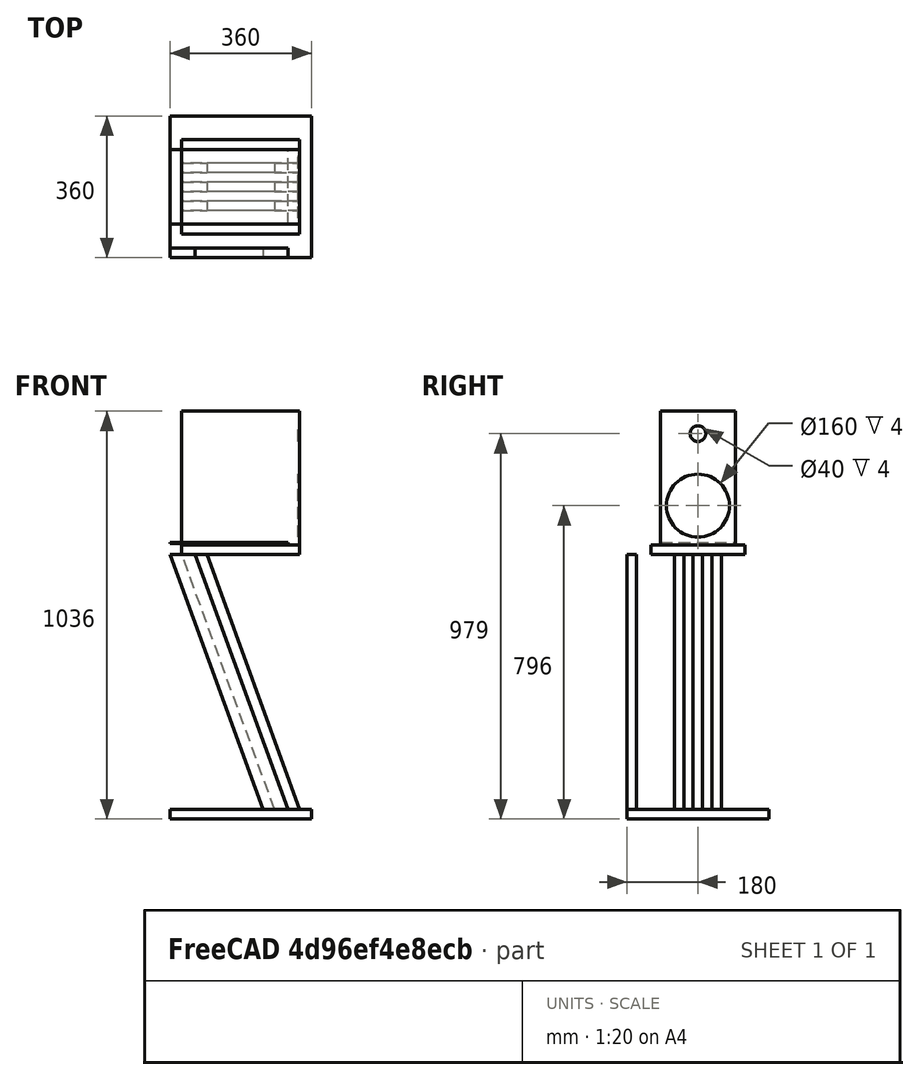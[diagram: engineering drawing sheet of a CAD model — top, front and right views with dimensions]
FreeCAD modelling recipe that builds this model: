
FCSTD DOCUMENT  (FreeCAD 0.18.4R)
Label: v3_3
License: All rights reserved
LicenseURL: http://en.wikipedia.org/wiki/All_rights_reserved
objects: Part::Box×6, Raytracing::RayFeature×6, Part::Feature×3, Part::Cylinder×2, Part::Cut×2, Part::MultiCommon×1, Raytracing::RayProject×1
note: 14 computed .brp shape members not serialized (recipe doc carries the construction recipe); baked Part::Feature solids carry a one-line shape summary decoded from their .brp

FEATURE [Part::Box] Box  label="Bottom"
  AttacherType = Attacher::AttachEngine3D
  Height = 24
  Length = 360
  Width = 360
FEATURE [Part::Box] Box003  label="SlipMate"
  AttacherType = Attacher::AttachEngine3D
  Height = 3
  Length = 300
  Placement = pos=(0,85,700) rot=(0,0,1;0rad)
  Width = 190
FEATURE [Part::Box] Box006  label="Speaker003"
  AttacherType = Attacher::AttachEngine3D
  Height = 340
  Length = 300
  Placement = pos=(0,0,850) rot=(0,0,1;0rad)
  Width = 190
FEATURE [Part::Cylinder] Cylinder002
  Angle = 360
  AttacherType = Attacher::AttachEngine3D
  Height = 10
  Placement = pos=(296,95,950) rot=(0,1,0;1.5708rad)
  Radius = 80
FEATURE [Part::Cut] Cut003
  Base = -> Box006
  Tool = -> Cylinder002
FEATURE [Part::Cylinder] Cylinder003
  Angle = 360
  AttacherType = Attacher::AttachEngine3D
  Height = 10
  Placement = pos=(296,95,1133) rot=(0,1,0;1.5708rad)
  Radius = 20
FEATURE [Part::Cut] Cut002  label="Speaker002"
  Base = -> Cut003
  Placement = pos=(30,85,-154) rot=(0,0,1;0rad)
  Tool = -> Cylinder003
FEATURE [Part::Box] Box012  label="Top"
  AttacherType = Attacher::AttachEngine3D
  Height = 24
  Length = 300
  Placement = pos=(30,60,672) rot=(0,0,1;0rad)
  Width = 240
FEATURE [Part::Box] Box015  label="Cube"
  AttacherType = Attacher::AttachEngine3D
  Height = 648
  Length = 300
  Placement = pos=(0,0,24) rot=(0,1,0;0rad)
  Width = 24
FEATURE [Part::Box] Box016  label="Cube007"
  AttacherType = Attacher::AttachEngine3D
  Height = 827
  Length = 60
  Placement = pos=(300,24,24) rot=(-0.173648,0,0.984808;3.14159rad)
  Width = 24
FEATURE [Part::MultiCommon] Common  label="Stand"
  Shapes = -> [Box015,Box016]
FEATURE [Part::Feature] Common_solid  label="Stand001"
  Placement = pos=(30,120,0) rot=(0,0,1;0rad)
  shape: bbox 299.7 x 24 x 648 mm, 6 faces (baked)
FEATURE [Part::Feature] Common_solid001  label="Stand002"
  Placement = pos=(30,168,0) rot=(0,0,1;0rad)
  shape: bbox 299.7 x 24 x 648 mm, 6 faces (baked)
FEATURE [Part::Feature] Common_solid002  label="Stand003"
  Placement = pos=(30,216,0) rot=(0,0,1;0rad)
  shape: bbox 299.7 x 24 x 648 mm, 6 faces (baked)
FEATURE [Raytracing::RayFeature] Common_solid_View
  Result = <blob: 3076 chars omitted>
  Source = -> Common_solid
  Transparency = 0
FEATURE [Raytracing::RayFeature] Common_solid002_View
  Result = <blob: 3038 chars omitted>
  Source = -> Common_solid002
  Transparency = 0
FEATURE [Raytracing::RayFeature] Common_solid001_View
  Result = <blob: 3038 chars omitted>
  Source = -> Common_solid001
  Transparency = 0
FEATURE [Raytracing::RayFeature] Box012_View
  Result = <blob: 2730 chars omitted>
  Source = -> Box012
  Transparency = 0
FEATURE [Raytracing::RayFeature] Box_View
  Result = <blob: 2628 chars omitted>
  Source = -> Box
  Transparency = 0
FEATURE [Raytracing::RayFeature] Cut002_View
  Result = <blob: 38202 chars omitted>
  Source = -> Cut002
  Transparency = 0
FEATURE [Raytracing::RayProject] PovProject
  Camera = // declares position and view direction\n\n// Generated by FreeCAD (http://www.freecadweb.org/)\n#declare cam_location =  <196.548,449.177,-1965.72>;\n#declare cam_look_at  = <187.259,521.851,359.314>;\n#declare cam_sky      = <-0.00274216,0.999508,-0.0312531>;\n#declare cam_angle    = 45; \ncamera {\n  location  cam_location\n  look_at   cam_look_at\n  sky       cam_sky\n  angle     cam_angle \n  right x*800/600\n}
  Group = -> [Common_solid_View,Common_solid002_View,Common_solid001_View,Box012_View,Box_View,Cut002_View]
  Template = <path>
note: 1 file-system path scrubbed to <path> (originals preserved in the JSON sidecar)
